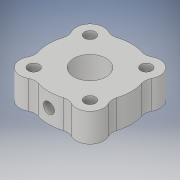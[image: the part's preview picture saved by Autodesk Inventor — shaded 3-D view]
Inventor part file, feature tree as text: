
AUTODESK INVENTOR PART (.ipt)
format: ipt  version: 2019 (Build 230136000, 136)  size: 147,968 bytes
history: native  units: mm
features: fillet x1
ambient origin geometry x8: Origin, YZ Plane, XZ Plane, XY Plane, X Axis, Y Axis, Z Axis, Center Point
bodies: Solid1 (feature_tree)
feature tree (1):
  fillet  "Fillet1"  [1 undecoded]
note: 1 required parameter value undecoded (feature->parameter linkage not recoverable at this tier; creation-order binding heuristic only, values carry confidence <= 0.55)
